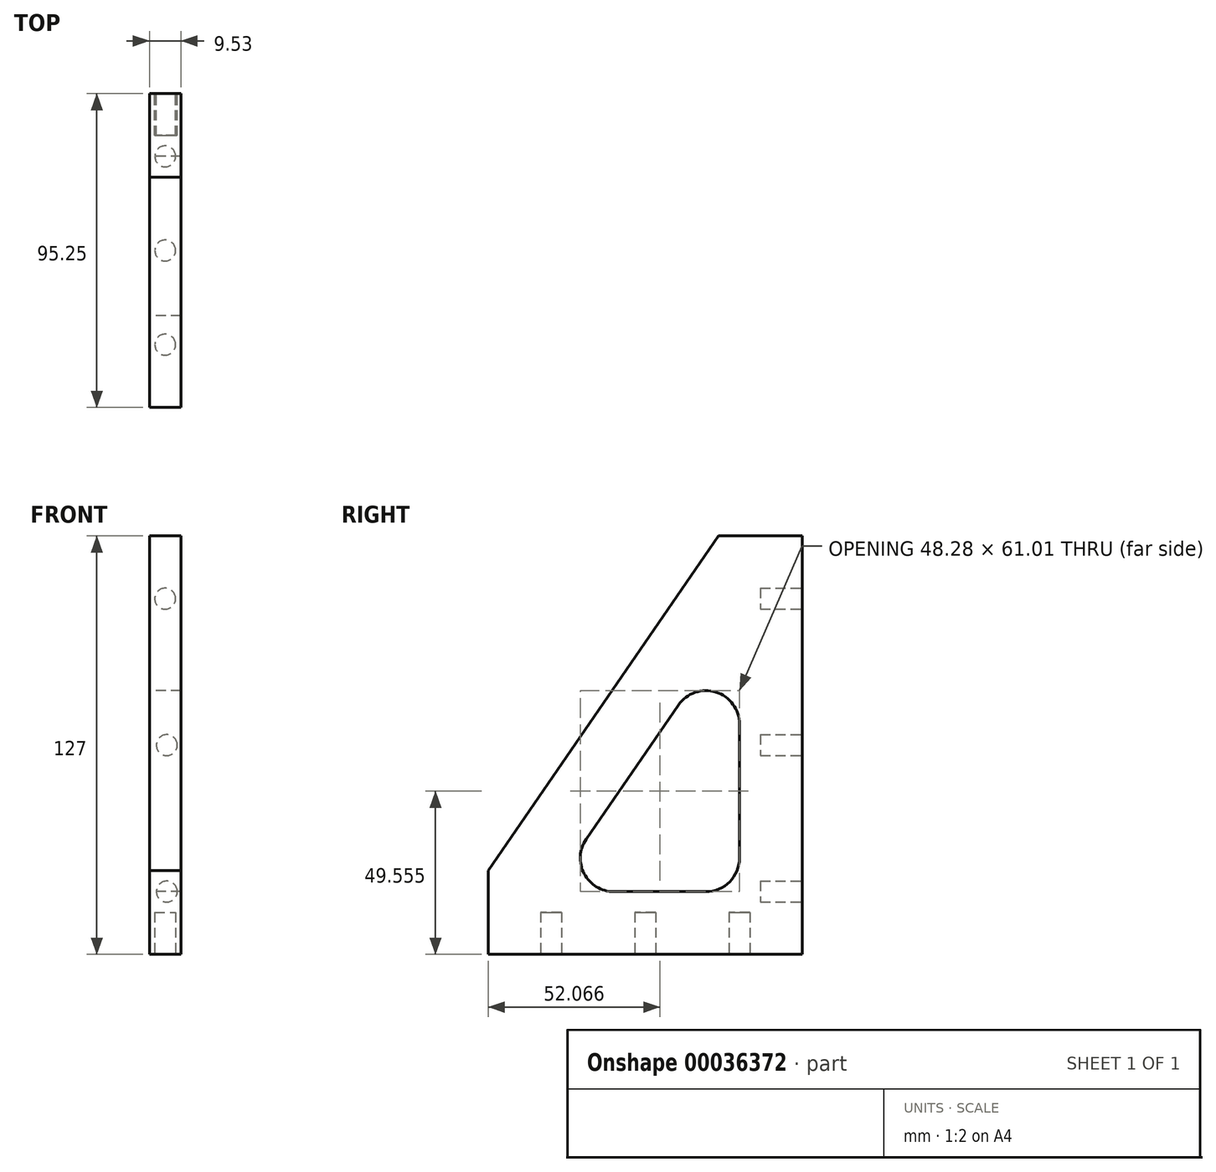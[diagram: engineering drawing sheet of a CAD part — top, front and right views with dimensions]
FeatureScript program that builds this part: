
annotation { "Feature Type Name" : "Feature", "Feature Type Description" : "" }
export const myFeature = defineFeature(function(context is Context, id is Id, definition is map)
    precondition{}
    {
        {
            var Q0;
            Q0=qCreatedBy(makeId("Right.planeOp"),FACE);
            var sketch = newSketch(context, id + "F0", { "sketchPlane" : qUnion([Q0])});
            skLineSegment(sketch, "E0", {"start": v(12.04, 46.13) * mm, "end": v(-13.36, 46.13) * mm});
            skLineSegment(sketch, "E1", {"start": v(12.04, 46.13) * mm, "end": v(12.04, -80.87) * mm});
            skLineSegment(sketch, "E2", {"start": v(12.04, -80.87) * mm, "end": v(-83.2, -80.87) * mm});
            skLineSegment(sketch, "E3", {"start": v(-83.2, -80.87) * mm, "end": v(-83.2, -55.47) * mm});
            skLineSegment(sketch, "E4", {"start": v(-13.36, 46.13) * mm, "end": v(-83.2, -55.47) * mm});
            skSolve(sketch);
        }
        {
            var Q0;
            Q0=makeQuery(id+"F0.imprint","IMPRINT",FACE,{"disambiguationData":[TD([[makeQuery(id+"F0.imprint","IMPRINT",EDGE,{"derivedFrom":sQuery(id+"F0.wireOp",EDGE,"E0")}),1.0]])]});
            extrude(context, id + "F1", {"entities" : qUnion([Q0]), "depth" : 9.52 * mm});
        }
        {
            var Q0;
            Q0=makeQuery(id+"F1.opExtrude","CAP_FACE",FACE,{"disambiguationData":[OSD([sQuery(id+"F0.wireOp",EDGE,"E0"),sQuery(id+"F0.wireOp",EDGE,"E1"),sQuery(id+"F0.wireOp",EDGE,"E2"),sQuery(id+"F0.wireOp",EDGE,"E3"),sQuery(id+"F0.wireOp",EDGE,"E4")])],"isStart":true});
            var sketch = newSketch(context, id + "F2", { "sketchPlane" : qUnion([Q0])});
            skLineSegment(sketch, "E5", {"start": v(7, -61.82) * mm, "end": v(64.45, -61.82) * mm});
            skLineSegment(sketch, "E6", {"start": v(7, 21.74) * mm, "end": v(64.45, -61.82) * mm});
            skLineSegment(sketch, "E7", {"start": v(7, 21.74) * mm, "end": v(7, -61.82) * mm});
            skSolve(sketch);
        }
        {
            var Q0;
            Q0 = qSketchRegion(id + "F2", true);
            extrude(context, id + "F3", {"entities" : qUnion([Q0]), "operationType" : NewBodyOperationType.REMOVE, "endBound" : BoundingType.THROUGH_ALL, "oppositeDirection" : true, "depth" : 25.4 * mm});
        }
        {
            var Q0;
            Q0=makeQuery(id+"F3.boolean.opBoolean","COPY",EDGE,{"derivedFrom":makeQuery(id+"F3.opExtrude","SWEPT_EDGE",EDGE,{"disambiguationData":[OSD([sQuery(id+"F2.wireOp",EDGE,"E5"),sQuery(id+"F2.wireOp",EDGE,"E7")])]})});
            fillet(context, id + "F4", {"entities" : qUnion([Q0]), "radius" : 10.16 * mm, "allowEdgeOverflow" : false});
        }
        {
            var Q0;
            Q0=makeQuery(id+"F3.boolean.opBoolean","COPY",EDGE,{"derivedFrom":makeQuery(id+"F3.opExtrude","SWEPT_EDGE",EDGE,{"disambiguationData":[OSD([sQuery(id+"F2.wireOp",EDGE,"E6"),sQuery(id+"F2.wireOp",EDGE,"E7")])]})});
            fillet(context, id + "F5", {"entities" : qUnion([Q0]), "radius" : 10.16 * mm, "tangentPropagation" : true, "allowEdgeOverflow" : false});
        }
        {
            var Q0;
            Q0=makeQuery(id+"F3.boolean.opBoolean","COPY",EDGE,{"derivedFrom":makeQuery(id+"F3.opExtrude","SWEPT_EDGE",EDGE,{"disambiguationData":[OSD([sQuery(id+"F2.wireOp",EDGE,"E5"),sQuery(id+"F2.wireOp",EDGE,"E6")])]})});
            fillet(context, id + "F6", {"entities" : qUnion([Q0]), "radius" : 10.16 * mm, "tangentPropagation" : true, "allowEdgeOverflow" : false});
        }
        {
            var Q0;
            Q0=makeQuery(id+"F1.opExtrude","SWEPT_FACE",FACE,{"disambiguationData":[OSD([sQuery(id+"F0.wireOp",EDGE,"E1")])]});
            var sketch = newSketch(context, id + "F7", { "sketchPlane" : qUnion([Q0])});
            skCircle(sketch, "E8", {"center": v(-4.75, 27.08) * mm, "radius": 3.18 * mm});
            skCircle(sketch, "E9", {"center": v(-5.24, -17.37) * mm, "radius": 3.18 * mm});
            skCircle(sketch, "E10", {"center": v(-5.24, -61.82) * mm, "radius": 3.18 * mm});
            skSolve(sketch);
        }
        {
            var Q0;
            Q0=makeQuery(id+"F1.opExtrude","SWEPT_FACE",FACE,{"disambiguationData":[OSD([sQuery(id+"F0.wireOp",EDGE,"E2")])]});
            var sketch = newSketch(context, id + "F8", { "sketchPlane" : qUnion([Q0])});
            skCircle(sketch, "E11", {"center": v(4.78, 7) * mm, "radius": 3.18 * mm});
            skCircle(sketch, "E12", {"center": v(4.78, 35.58) * mm, "radius": 3.18 * mm});
            skCircle(sketch, "E13", {"center": v(4.78, 64.16) * mm, "radius": 3.18 * mm});
            skSolve(sketch);
        }
        {
            var Q0;
            Q0=makeQuery(id+"F7.imprint","IMPRINT",FACE,{"disambiguationData":[TD([[makeQuery(id+"F7.imprint","IMPRINT",EDGE,{"derivedFrom":sQuery(id+"F7.wireOp",EDGE,"E9")}),1.0]])]});
            var Q1;
            Q1=makeQuery(id+"F7.imprint","IMPRINT",FACE,{"disambiguationData":[TD([[makeQuery(id+"F7.imprint","IMPRINT",EDGE,{"derivedFrom":sQuery(id+"F7.wireOp",EDGE,"E10")}),1.0]])]});
            var Q2;
            Q2=makeQuery(id+"F7.imprint","IMPRINT",FACE,{"disambiguationData":[TD([[makeQuery(id+"F7.imprint","IMPRINT",EDGE,{"derivedFrom":sQuery(id+"F7.wireOp",EDGE,"E8")}),1.0]])]});
            extrude(context, id + "F9", {"entities" : qUnion([Q0, Q1, Q2]), "operationType" : NewBodyOperationType.REMOVE, "oppositeDirection" : true, "depth" : 12.7 * mm});
        }
        {
            var Q0;
            Q0 = qSketchRegion(id + "F8", true);
            extrude(context, id + "F10", {"entities" : qUnion([Q0]), "operationType" : NewBodyOperationType.REMOVE, "oppositeDirection" : true, "depth" : 12.7 * mm});
        }
    });
